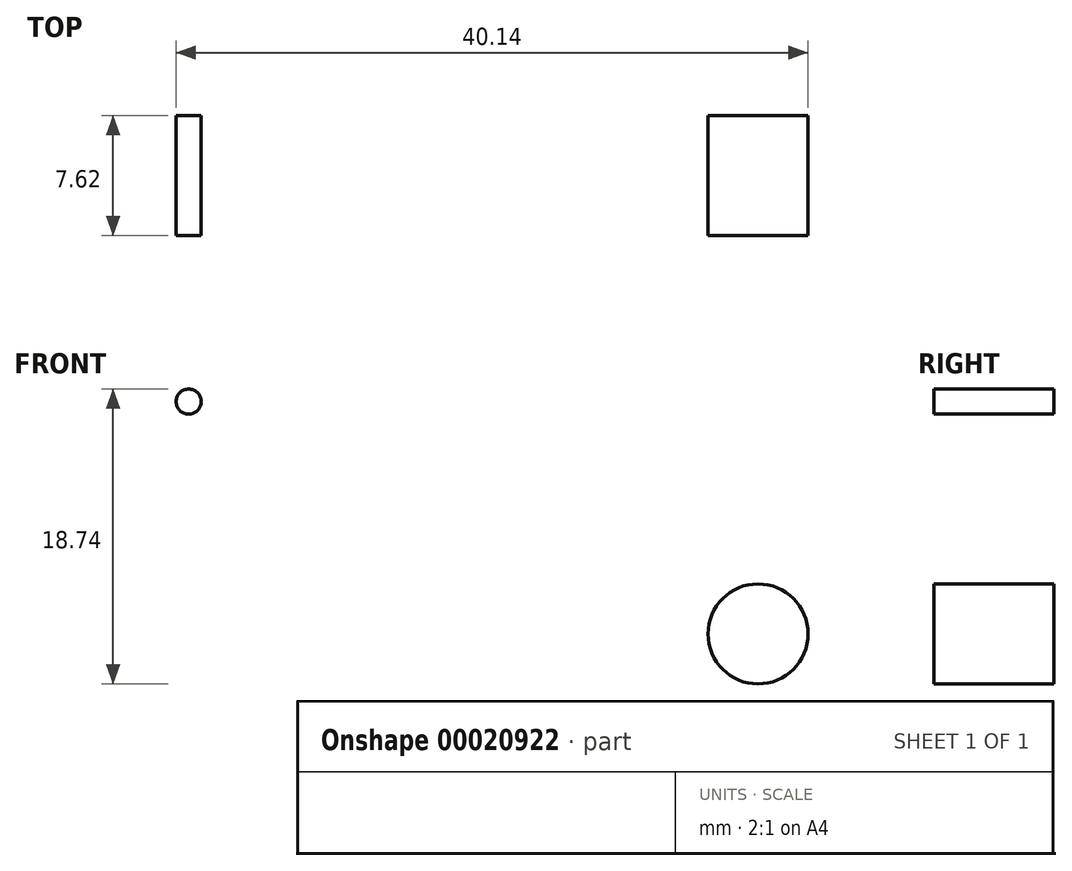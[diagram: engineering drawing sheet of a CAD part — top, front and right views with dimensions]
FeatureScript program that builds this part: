
annotation { "Feature Type Name" : "Feature", "Feature Type Description" : "" }
export const myFeature = defineFeature(function(context is Context, id is Id, definition is map)
    precondition{}
    {
        {
            var Q0;
            Q0=qCreatedBy(makeId("Front.planeOp"),FACE);
            var sketch = newSketch(context, id + "F0", { "sketchPlane" : qUnion([Q0])});
            skCircle(sketch, "E0", {"center": v(0, 0) * mm, "radius": 3.18 * mm});
            skCircle(sketch, "E1", {"center": v(-36.16, 14.76) * mm, "radius": 0.8 * mm});
            skSolve(sketch);
        }
        {
            var Q0;
            Q0 = qSketchRegion(id + "F0", true);
            extrude(context, id + "F1", {"entities" : qUnion([Q0]), "depth" : 7.62 * mm});
        }
    });
